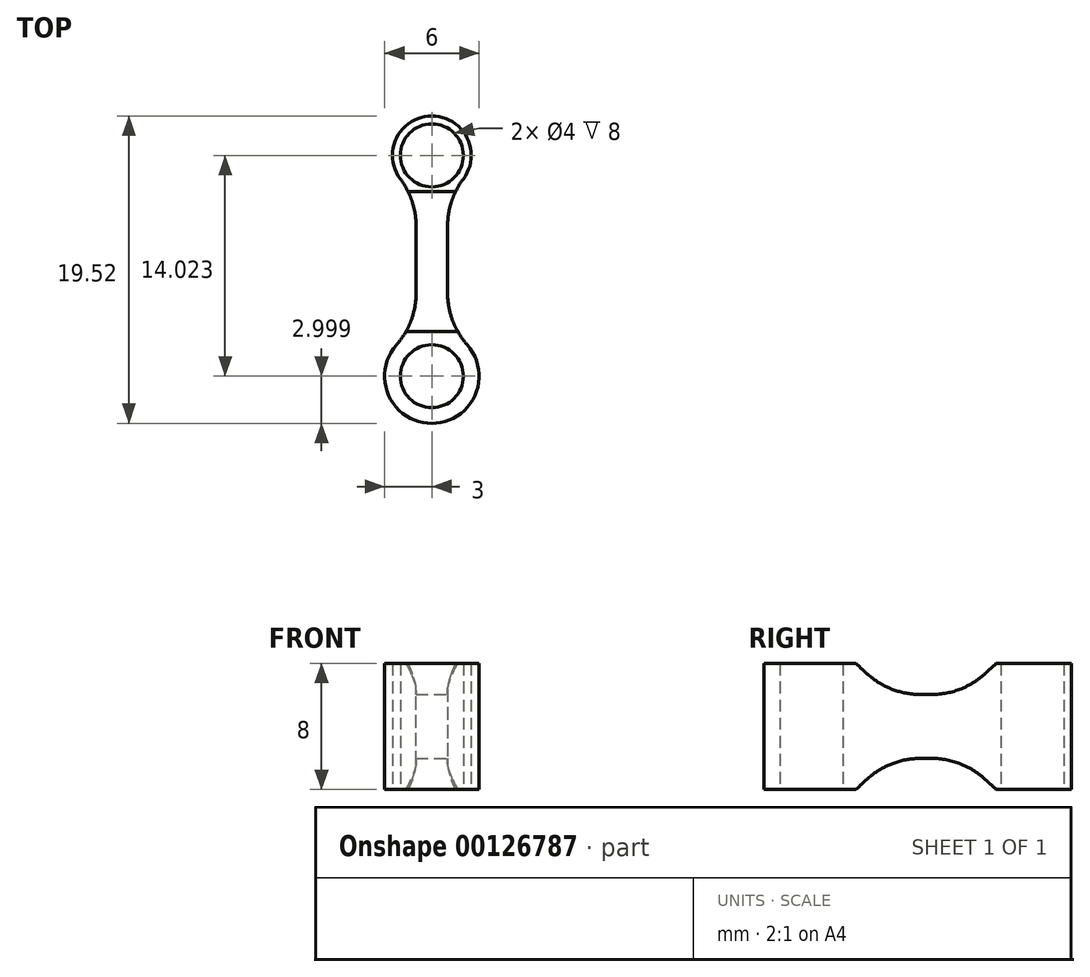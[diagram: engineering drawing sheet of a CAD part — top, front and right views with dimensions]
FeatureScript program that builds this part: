
annotation { "Feature Type Name" : "Feature", "Feature Type Description" : "" }
export const myFeature = defineFeature(function(context is Context, id is Id, definition is map)
    precondition{}
    {
        {
            var Q0;
            Q0=qCreatedBy(makeId("Top.planeOp"),FACE);
            var sketch = newSketch(context, id + "F0", { "sketchPlane" : qUnion([Q0])});
            skCircle(sketch, "E0", {"center": v(0, 28.4) * mm, "radius": 2 * mm});
            skArc(sketch, "E1", {"start": v(1, 26.1) * mm, "mid": v(0, 30.9) * mm, "end": v(-1, 26.1) * mm});
            skArc(sketch, "E2", {"start": v(-1, 17.2) * mm, "mid": v(0, 11.37) * mm, "end": v(1, 17.2) * mm});
            skCircle(sketch, "E3", {"center": v(0, 14.37) * mm, "radius": 2 * mm});
            skLineSegment(sketch, "E4", {"start": v(-1, 26.1) * mm, "end": v(-1, 17.2) * mm});
            skLineSegment(sketch, "E5", {"start": v(1, 26.1) * mm, "end": v(1, 17.2) * mm});
            skLineSegment(sketch, "E6", {"start": v(0, 28.4) * mm, "end": v(-1, 26.1) * mm, "construction": true});
            skLineSegment(sketch, "E7", {"start": v(0, 28.4) * mm, "end": v(1, 26.1) * mm, "construction": true});
            skLineSegment(sketch, "E8", {"start": v(0, 14.37) * mm, "end": v(-1, 17.2) * mm, "construction": true});
            skLineSegment(sketch, "E9", {"start": v(0, 14.37) * mm, "end": v(1, 17.2) * mm, "construction": true});
            skSolve(sketch);
        }
        {
            var Q0;
            Q0=makeQuery(id+"F0.imprint","IMPRINT",FACE,{"disambiguationData":[TD([[makeQuery(id+"F0.imprint","IMPRINT",EDGE,{"derivedFrom":sQuery(id+"F0.wireOp",EDGE,"E0")}),-1.0]])]});
            extrude(context, id + "F1", {"entities" : qUnion([Q0]), "depth" : 8 * mm});
        }
        {
            var Q0;
            Q0=makeQuery(id+"F1.opExtrude","SWEPT_FACE",FACE,{"disambiguationData":[OSD([sQuery(id+"F0.wireOp",EDGE,"E5")])]});
            var sketch = newSketch(context, id + "F2", { "sketchPlane" : qUnion([Q0])});
            skLineSegment(sketch, "E10", {"start": v(26.1, 4) * mm, "end": v(10.16, 4) * mm, "construction": true});
            skPoint(sketch, "E11", {"position": v(18.13, 4) * mm});
            skLineSegment(sketch, "E12", {"start": v(26.1, 8) * mm, "end": v(23.96, 6.03) * mm});
            skLineSegment(sketch, "E13", {"start": v(23.96, 6.03) * mm, "end": v(19.34, 6.03) * mm});
            skLineSegment(sketch, "E14", {"start": v(19.34, 6.03) * mm, "end": v(17.2, 8) * mm});
            skLineSegment(sketch, "E15", {"start": v(26.1, 0) * mm, "end": v(23.96, 1.97) * mm});
            skLineSegment(sketch, "E16", {"start": v(23.96, 1.97) * mm, "end": v(19.34, 1.97) * mm});
            skLineSegment(sketch, "E17", {"start": v(19.34, 1.97) * mm, "end": v(17.2, 0) * mm});
            skLineSegment(sketch, "E18", {"start": v(23.97, 11.17) * mm, "end": v(23.97, -5.39) * mm, "construction": true});
            skLineSegment(sketch, "E19", {"start": v(19.3, 11.38) * mm, "end": v(19.3, -4.85) * mm, "construction": true});
            skSolve(sketch);
        }
        {
            var Q0;
            Q0=makeQuery(id+"F2.imprint","IMPRINT",FACE,{"disambiguationData":[TD([[makeQuery(id+"F2.imprint","IMPRINT",EDGE,{"derivedFrom":sQuery(id+"F2.wireOp",EDGE,"E12")}),-1.0]])]});
            var Q1;
            Q1=makeQuery(id+"F2.imprint","IMPRINT",FACE,{"disambiguationData":[TD([[makeQuery(id+"F2.imprint","IMPRINT",EDGE,{"derivedFrom":sQuery(id+"F2.wireOp",EDGE,"E15")}),1.0]])]});
            extrude(context, id + "F3", {"entities" : qUnion([Q0, Q1]), "operationType" : NewBodyOperationType.REMOVE, "oppositeDirection" : true, "depth" : 25 * mm});
        }
        {
            var Q0;
            Q0=makeQuery(id+"F1.opExtrude","SWEPT_EDGE",EDGE,{"disambiguationData":[OSD([sQuery(id+"F0.wireOp",EDGE,"E1"),sQuery(id+"F0.wireOp",EDGE,"E5")])]});
            var Q1;
            Q1=makeQuery(id+"F1.opExtrude","SWEPT_EDGE",EDGE,{"disambiguationData":[OSD([sQuery(id+"F0.wireOp",EDGE,"E2"),sQuery(id+"F0.wireOp",EDGE,"E5")])]});
            var Q2;
            Q2=makeQuery(id+"F1.opExtrude","SWEPT_EDGE",EDGE,{"disambiguationData":[OSD([sQuery(id+"F0.wireOp",EDGE,"E1"),sQuery(id+"F0.wireOp",EDGE,"E4")])]});
            var Q3;
            Q3=makeQuery(id+"F1.opExtrude","SWEPT_EDGE",EDGE,{"disambiguationData":[OSD([sQuery(id+"F0.wireOp",EDGE,"E2"),sQuery(id+"F0.wireOp",EDGE,"E4")])]});
            fillet(context, id + "F4", {"entities" : qUnion([Q0, Q1, Q2, Q3]), "radius" : 5 * mm, "tangentPropagation" : true, "allowEdgeOverflow" : false});
        }
        {
            var Q0;
            Q0=makeQuery(id+"F3.boolean.opBoolean","COPY",EDGE,{"derivedFrom":makeQuery(id+"F3.opExtrude","SWEPT_EDGE",EDGE,{"disambiguationData":[OSD([sQuery(id+"F2.wireOp",EDGE,"E12"),sQuery(id+"F2.wireOp",EDGE,"E13")])]})});
            var Q1;
            Q1=makeQuery(id+"F3.boolean.opBoolean","COPY",EDGE,{"derivedFrom":makeQuery(id+"F3.opExtrude","SWEPT_EDGE",EDGE,{"disambiguationData":[OSD([sQuery(id+"F2.wireOp",EDGE,"E13"),sQuery(id+"F2.wireOp",EDGE,"E14")])]})});
            var Q2;
            Q2=makeQuery(id+"F3.boolean.opBoolean","COPY",EDGE,{"derivedFrom":makeQuery(id+"F3.opExtrude","SWEPT_EDGE",EDGE,{"disambiguationData":[OSD([sQuery(id+"F2.wireOp",EDGE,"E15"),sQuery(id+"F2.wireOp",EDGE,"E16")])]})});
            var Q3;
            Q3=makeQuery(id+"F3.boolean.opBoolean","COPY",EDGE,{"derivedFrom":makeQuery(id+"F3.opExtrude","SWEPT_EDGE",EDGE,{"disambiguationData":[OSD([sQuery(id+"F2.wireOp",EDGE,"E16"),sQuery(id+"F2.wireOp",EDGE,"E17")])]})});
            fillet(context, id + "F5", {"entities" : qUnion([Q0, Q1, Q2, Q3]), "radius" : 5 * mm, "tangentPropagation" : true, "allowEdgeOverflow" : false});
        }
    });
